# Revit family: 76220XXX_NEW
name_source: partatom
category: Plumbing Fixtures
revit_build: Autodesk Revit 2018 (Build: 20170223_1515(x64)
units: mm (PartAtom-declared; Revit-internal decimal feet)

## family parameters
Always vertical = No
Cut with Voids When Loaded = No
Part Type = Normal
Room Calculation Point = No
Round Connector Dimension = Use Diameter
Shared = No
Work Plane-Based = Yes

## types (2) — shared parameters
Always visible = Yes
BIMobject category = Wash Basins
Default Elevation = 1219.2 mm  [stored 4 ft]
Design country = Germany
EAN code = 4059625395219
Edition number = 1
GTIN code = https://4059625395219
IFC Classification = Sanitary Terminal
Installation instructions = https://www.hansgrohe.com
Manufacturer country = Germany
Manufacturer name = hansgrohe
Material 2 = Hansgrohe - Finoris - Gray
NBS Reference Code = 31-75
NBS Reference Description = Sanitary Accessories
Product Guid = fd11189f-3cea-43b9-8335-d9248109eb55
Product SKU = 76220XXX
Product data url = https://www.bimobject.com
Product family = Finoris
Product group = Basin mixers
Product name = 76220XXX Finoris Single lever basin mixer 260 with bidette hand shower and shower hose 160 cm
Product url = https://www.hansgrohe.com
QR code = https://www.bimobject.com
Technical description = https://www.hansgrohe.com
UNSPSC Code = 301815

## per-type parameters (varying)
| type | Material 1 |
| 670 Matte Black | Hansgrohe - Finoris - 670 Matte Black |
| 000 Chrome | Hansgrohe - Finoris - 000 Chrome |

note: [stored X ft] marks values corroborated as IEEE doubles in the binary element streams (Revit-internal decimal feet)

## geometry (parser evidence)
native form markers: Sweep x3
no freeform markers — native parametric forms only
